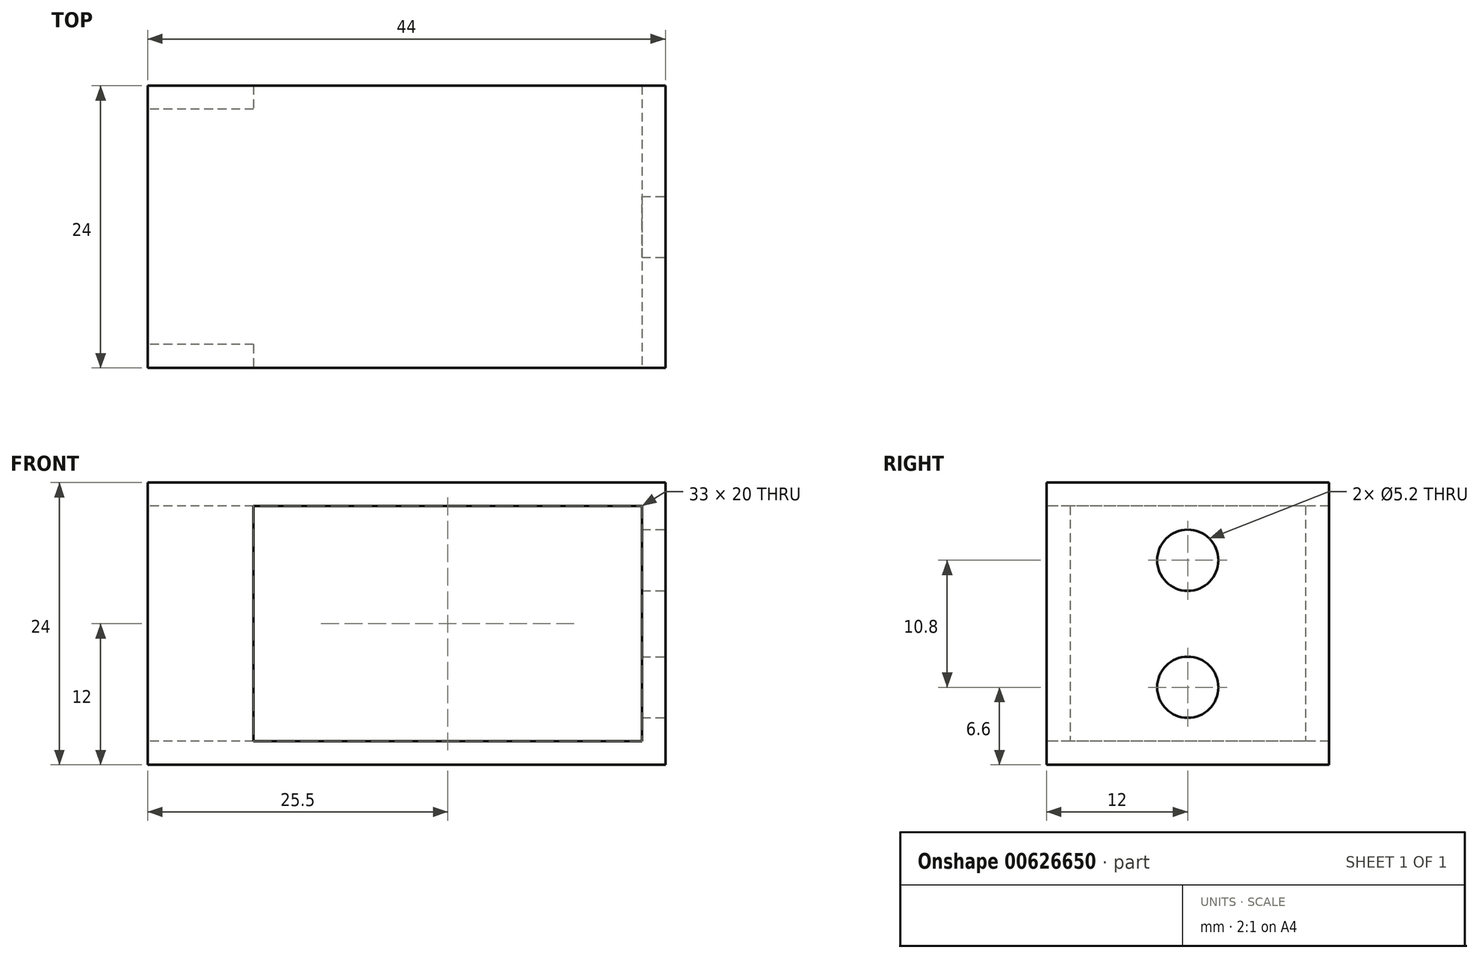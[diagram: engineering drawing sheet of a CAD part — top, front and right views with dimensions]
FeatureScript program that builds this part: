
annotation { "Feature Type Name" : "Feature", "Feature Type Description" : "" }
export const myFeature = defineFeature(function(context is Context, id is Id, definition is map)
    precondition{}
    {
        {
            var Q0;
            Q0=qCreatedBy(makeId("Right.planeOp"),FACE);
            var sketch = newSketch(context, id + "F0", { "sketchPlane" : qUnion([Q0])});
            skLineSegment(sketch, "E0.bottom", {"start": v(12, -12) * mm, "end": v(-12, -12) * mm});
            skLineSegment(sketch, "E0.top", {"start": v(12, 12) * mm, "end": v(-12, 12) * mm});
            skLineSegment(sketch, "E0.left", {"start": v(12, -12) * mm, "end": v(12, 12) * mm});
            skLineSegment(sketch, "E0.right", {"start": v(-12, -12) * mm, "end": v(-12, 12) * mm});
            skPoint(sketch, "E0.middle", {"position": v(0, 0) * mm});
            skLineSegment(sketch, "E1.bottom", {"start": v(10, -10) * mm, "end": v(-10, -10) * mm});
            skLineSegment(sketch, "E1.top", {"start": v(10, 10) * mm, "end": v(-10, 10) * mm});
            skLineSegment(sketch, "E1.left", {"start": v(10, -10) * mm, "end": v(10, 10) * mm});
            skLineSegment(sketch, "E1.right", {"start": v(-10, -10) * mm, "end": v(-10, 10) * mm});
            skSolve(sketch);
        }
        {
            var Q0;
            Q0=makeQuery(id+"F0.imprint","IMPRINT",FACE,{"disambiguationData":[TD([[makeQuery(id+"F0.imprint","IMPRINT",EDGE,{"derivedFrom":sQuery(id+"F0.wireOp",EDGE,"E0.bottom")}),-1.0]])]});
            extrude(context, id + "F1", {"entities" : qUnion([Q0]), "depth" : 42 * mm, "offsetDistance" : 25 * mm});
        }
        {
            var Q0;
            Q0=makeQuery(id+"F1.opExtrude","SWEPT_FACE",FACE,{"disambiguationData":[OSD([sQuery(id+"F0.wireOp",EDGE,"E0.right")])]});
            var sketch = newSketch(context, id + "F2", { "sketchPlane" : qUnion([Q0])});
            skLineSegment(sketch, "E2.bottom", {"start": v(42, 10) * mm, "end": v(9, 10) * mm});
            skLineSegment(sketch, "E2.top", {"start": v(42, -10) * mm, "end": v(9, -10) * mm});
            skLineSegment(sketch, "E2.left", {"start": v(42, 10) * mm, "end": v(42, -10) * mm});
            skLineSegment(sketch, "E2.right", {"start": v(9, 10) * mm, "end": v(9, -10) * mm});
            skSolve(sketch);
        }
        {
            var Q0;
            Q0=makeQuery(id+"F2.imprint","IMPRINT",FACE,{"disambiguationData":[TD([[makeQuery(id+"F2.imprint","IMPRINT",EDGE,{"derivedFrom":sQuery(id+"F2.wireOp",EDGE,"E2.bottom")}),1.0]])]});
            extrude(context, id + "F3", {"entities" : qUnion([Q0]), "operationType" : NewBodyOperationType.REMOVE, "oppositeDirection" : true, "depth" : 31.3 * mm, "offsetDistance" : 25 * mm});
        }
        {
            var Q0;
            {var subQ0=sQuery(id+"F0.wireOp",EDGE,"E1.top");var subQ1=sQuery(id+"F0.wireOp",EDGE,"E0.right");var subQ2=sQuery(id+"F0.wireOp",EDGE,"E0.left");var subQ3=sQuery(id+"F0.wireOp",EDGE,"E0.top");Q0=makeQuery(id+"F3.boolean.opBoolean","SPLIT",FACE,{"disambiguationData":[TD([makeQuery(id+"F1.opExtrude","SWEPT_FACE",FACE,{"disambiguationData":[OSD([subQ3])]})])],"derivedFrom":makeQuery(id+"F1.opExtrude","CAP_FACE",FACE,{"disambiguationData":[OSD([sQuery(id+"F0.wireOp",EDGE,"E0.bottom"),subQ3,subQ2,subQ1,sQuery(id+"F0.wireOp",EDGE,"E1.bottom"),subQ0,sQuery(id+"F0.wireOp",EDGE,"E1.left"),sQuery(id+"F0.wireOp",EDGE,"E1.right")])],"isStart":false})});}
            var sketch = newSketch(context, id + "F4", { "sketchPlane" : qUnion([Q0])});
            skLineSegment(sketch, "E3.bottom", {"start": v(12, 12) * mm, "end": v(-12, 12) * mm});
            skLineSegment(sketch, "E3.top", {"start": v(12, -12) * mm, "end": v(-12, -12) * mm});
            skLineSegment(sketch, "E3.left", {"start": v(12, 12) * mm, "end": v(12, -12) * mm});
            skLineSegment(sketch, "E3.right", {"start": v(-12, 12) * mm, "end": v(-12, -12) * mm});
            skSolve(sketch);
        }
        {
            var Q0;
            {var subQ0=sQuery(id+"F4.wireOp",EDGE,"E3.top");Q0=makeQuery(id+"F4.imprint","IMPRINT",FACE,{"disambiguationData":[TD([[makeQuery(id+"F4.imprint","IMPRINT",EDGE,{"derivedFrom":subQ0}),-1.0]])]});}
            var Q1;
            {var subQ0=sQuery(id+"F4.wireOp",EDGE,"E3.bottom");Q1=makeQuery(id+"F4.imprint","IMPRINT",FACE,{"disambiguationData":[TD([[makeQuery(id+"F4.imprint","IMPRINT",EDGE,{"derivedFrom":subQ0}),1.0]])]});}
            extrude(context, id + "F5", {"entities" : qUnion([Q0, Q1]), "operationType" : NewBodyOperationType.ADD, "depth" : 2 * mm, "offsetDistance" : 25 * mm});
        }
        {
            var Q0;
            Q0=makeQuery(id+"F5.opExtrude","CAP_FACE",FACE,{"disambiguationData":[OSD([sQuery(id+"F4.wireOp",EDGE,"E3.bottom"),sQuery(id+"F4.wireOp",EDGE,"E3.top"),sQuery(id+"F4.wireOp",EDGE,"E3.left"),sQuery(id+"F4.wireOp",EDGE,"E3.right")])],"isStart":false});
            var sketch = newSketch(context, id + "F6", { "sketchPlane" : qUnion([Q0])});
            skCircle(sketch, "E4", {"center": v(0, 5.4) * mm, "radius": 2.6 * mm});
            skCircle(sketch, "E5", {"center": v(0, -5.4) * mm, "radius": 2.6 * mm});
            skSolve(sketch);
        }
        {
            var Q0;
            Q0=makeQuery(id+"F6.imprint","IMPRINT",FACE,{"disambiguationData":[TD([[makeQuery(id+"F6.imprint","IMPRINT",EDGE,{"derivedFrom":sQuery(id+"F6.wireOp",EDGE,"E4")}),1.0]])]});
            var Q1;
            Q1=makeQuery(id+"F6.imprint","IMPRINT",FACE,{"disambiguationData":[TD([[makeQuery(id+"F6.imprint","IMPRINT",EDGE,{"derivedFrom":sQuery(id+"F6.wireOp",EDGE,"E5")}),1.0]])]});
            extrude(context, id + "F7", {"entities" : qUnion([Q0, Q1]), "operationType" : NewBodyOperationType.REMOVE, "oppositeDirection" : true, "depth" : 25 * mm, "offsetDistance" : 25 * mm});
        }
    });
